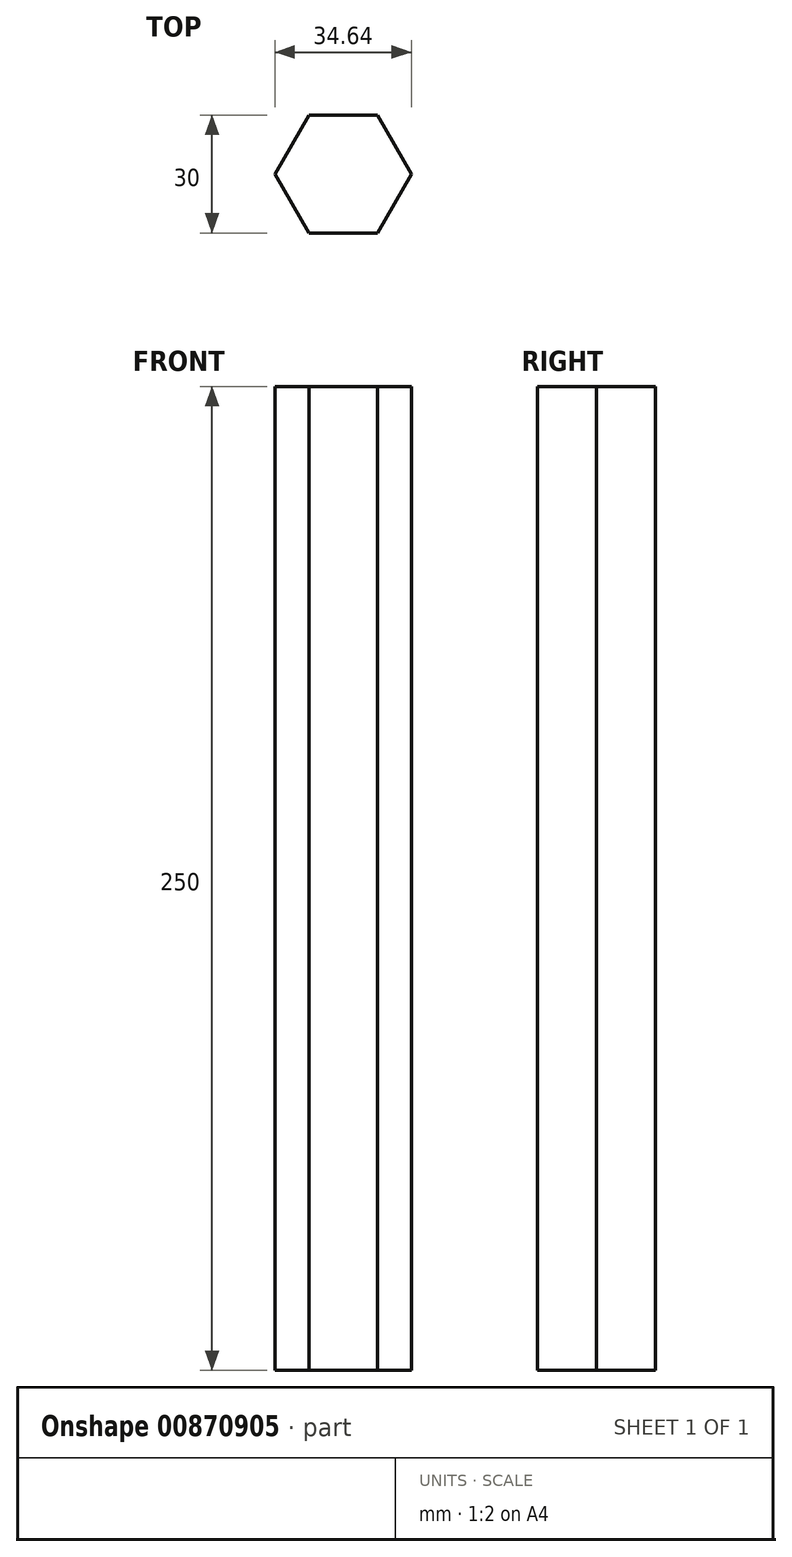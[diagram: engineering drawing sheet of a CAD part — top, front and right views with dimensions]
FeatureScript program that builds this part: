
annotation { "Feature Type Name" : "Feature", "Feature Type Description" : "" }
export const myFeature = defineFeature(function(context is Context, id is Id, definition is map)
    precondition{}
    {
        {
            var Q0;
            Q0=qCreatedBy(makeId("Top.planeOp"),FACE);
            var sketch = newSketch(context, id + "F0", { "sketchPlane" : qUnion([Q0])});
            skCircle(sketch, "E0.cCircle", {"center": v(0, 0) * mm, "radius": 15 * mm, "construction": true});
            skLineSegment(sketch, "E0.0", {"start": v(-8.66, 15) * mm, "end": v(8.66, 15) * mm});
            skLineSegment(sketch, "E0.1", {"start": v(8.66, 15) * mm, "end": v(17.32, 0) * mm});
            skLineSegment(sketch, "E0.2", {"start": v(17.32, 0) * mm, "end": v(8.66, -15) * mm});
            skLineSegment(sketch, "E0.3", {"start": v(8.66, -15) * mm, "end": v(-8.66, -15) * mm});
            skLineSegment(sketch, "E0.4", {"start": v(-8.66, -15) * mm, "end": v(-17.32, 0) * mm});
            skLineSegment(sketch, "E0.5", {"start": v(-17.32, 0) * mm, "end": v(-8.66, 15) * mm});
            skPoint(sketch, "E0.0.midPoint", {"position": v(0, 15) * mm});
            skSolve(sketch);
        }
        {
            var Q0;
            Q0=makeQuery(id+"F0.imprint","IMPRINT",FACE,{"disambiguationData":[TD([[makeQuery(id+"F0.imprint","IMPRINT",EDGE,{"derivedFrom":sQuery(id+"F0.wireOp",EDGE,"E0.0")}),-1.0]])]});
            extrude(context, id + "F1", {"entities" : qUnion([Q0]), "depth" : 250 * mm, "offsetDistance" : 25 * mm});
        }
    });
